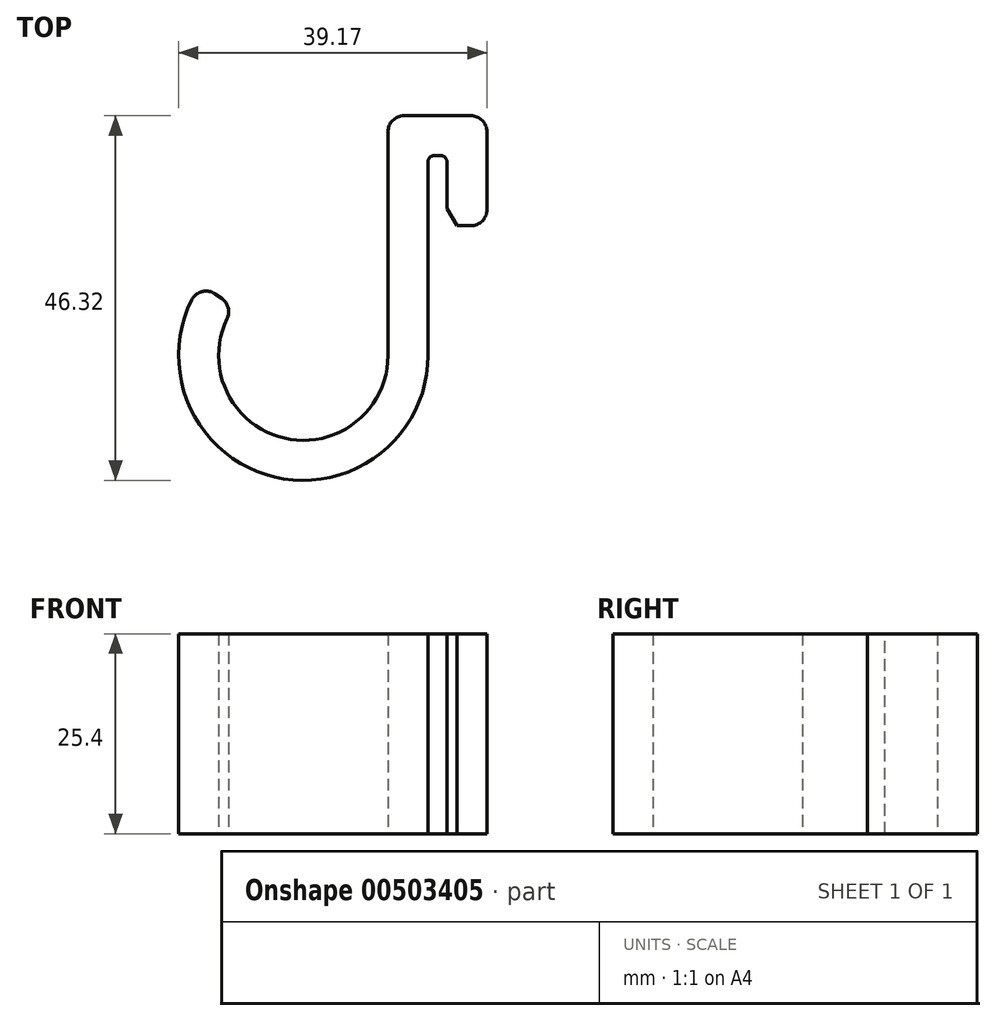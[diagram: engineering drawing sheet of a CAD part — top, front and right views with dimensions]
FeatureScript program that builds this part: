
annotation { "Feature Type Name" : "Feature", "Feature Type Description" : "" }
export const myFeature = defineFeature(function(context is Context, id is Id, definition is map)
    precondition{}
    {
        {
            var Q0;
            Q0=qCreatedBy(makeId("Top.planeOp"),FACE);
            var sketch = newSketch(context, id + "F0", { "sketchPlane" : qUnion([Q0])});
            skArc(sketch, "E0", {"start": v(-8.81, 6.17) * mm, "mid": v(-3.23, -10.26) * mm, "end": v(10.76, 0) * mm});
            skLineSegment(sketch, "E1", {"start": v(10.76, 0) * mm, "end": v(10.76, 30.48) * mm});
            skLineSegment(sketch, "E2", {"start": v(10.76, 30.48) * mm, "end": v(23.33, 30.48) * mm});
            skLineSegment(sketch, "E3", {"start": v(23.33, 30.48) * mm, "end": v(23.33, 16.51) * mm});
            skLineSegment(sketch, "E4", {"start": v(23.33, 16.51) * mm, "end": v(18.25, 16.51) * mm});
            skLineSegment(sketch, "E5", {"start": v(18.25, 16.51) * mm, "end": v(18.25, 25.4) * mm});
            skLineSegment(sketch, "E6", {"start": v(18.25, 25.4) * mm, "end": v(15.84, 25.4) * mm});
            skLineSegment(sketch, "E7", {"start": v(15.84, 25.4) * mm, "end": v(15.84, 0) * mm});
            skArc(sketch, "E8", {"start": v(-12.97, 9.08) * mm, "mid": v(-4.76, -15.1) * mm, "end": v(15.84, 0) * mm});
            skLineSegment(sketch, "E9", {"start": v(-8.81, 6.17) * mm, "end": v(-12.97, 9.08) * mm});
            skSolve(sketch);
        }
        {
            var Q0;
            Q0 = qSketchRegion(id + "F0", true);
            extrude(context, id + "F1", {"entities" : qUnion([Q0]), "depth" : 25.4 * mm});
        }
        {
            var Q0;
            Q0=makeQuery(id+"F1.opExtrude","SWEPT_EDGE",EDGE,{"disambiguationData":[OSD([sQuery(id+"F0.wireOp",EDGE,"E6"),sQuery(id+"F0.wireOp",EDGE,"E7")])]});
            var Q1;
            Q1=makeQuery(id+"F1.opExtrude","SWEPT_EDGE",EDGE,{"disambiguationData":[OSD([sQuery(id+"F0.wireOp",EDGE,"E5"),sQuery(id+"F0.wireOp",EDGE,"E6")])]});
            fillet(context, id + "F2", {"entities" : qUnion([Q0, Q1]), "radius" : 0.76 * mm, "tangentPropagation" : true, "allowEdgeOverflow" : false});
        }
        {
            var Q0;
            Q0=makeQuery(id+"F1.opExtrude","SWEPT_EDGE",EDGE,{"disambiguationData":[OSD([sQuery(id+"F0.wireOp",EDGE,"E3"),sQuery(id+"F0.wireOp",EDGE,"E4")])]});
            var Q1;
            Q1=makeQuery(id+"F1.opExtrude","SWEPT_EDGE",EDGE,{"disambiguationData":[OSD([sQuery(id+"F0.wireOp",EDGE,"E2"),sQuery(id+"F0.wireOp",EDGE,"E3")])]});
            var Q2;
            Q2=makeQuery(id+"F1.opExtrude","SWEPT_EDGE",EDGE,{"disambiguationData":[OSD([sQuery(id+"F0.wireOp",EDGE,"E1"),sQuery(id+"F0.wireOp",EDGE,"E2")])]});
            var Q3;
            Q3=makeQuery(id+"F1.opExtrude","SWEPT_EDGE",EDGE,{"disambiguationData":[OSD([sQuery(id+"F0.wireOp",EDGE,"E0"),sQuery(id+"F0.wireOp",EDGE,"E9")])]});
            var Q4;
            Q4=makeQuery(id+"F1.opExtrude","SWEPT_EDGE",EDGE,{"disambiguationData":[OSD([sQuery(id+"F0.wireOp",EDGE,"E8"),sQuery(id+"F0.wireOp",EDGE,"E9")])]});
            fillet(context, id + "F3", {"entities" : qUnion([Q0, Q1, Q2, Q3, Q4]), "radius" : 2.03 * mm, "tangentPropagation" : true, "allowEdgeOverflow" : false});
        }
        {
            var Q0;
            Q0=makeQuery(id+"F1.opExtrude","SWEPT_EDGE",EDGE,{"disambiguationData":[OSD([sQuery(id+"F0.wireOp",EDGE,"E4"),sQuery(id+"F0.wireOp",EDGE,"E5")])]});
            chamfer(context, id + "F4", {"entities" : qUnion([Q0]), "chamferType" : ChamferType.OFFSET_ANGLE, "width" : 1.27 * mm, "oppositeDirection" : false, "angle" : 60 * degree, "tangentPropagation" : true});
        }
    });
